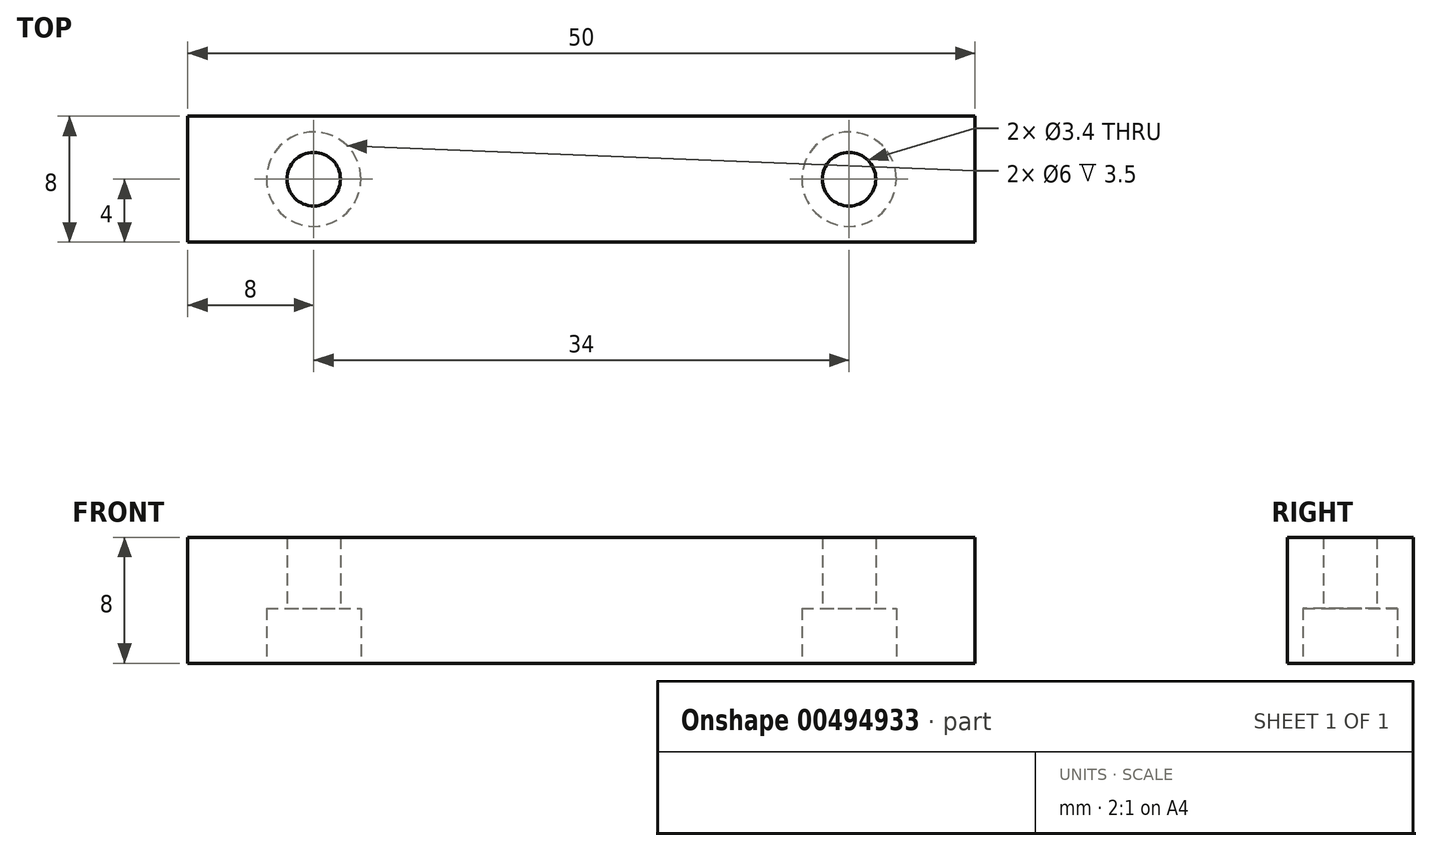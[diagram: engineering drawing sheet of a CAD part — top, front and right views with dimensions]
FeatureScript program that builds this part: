
annotation { "Feature Type Name" : "Feature", "Feature Type Description" : "" }
export const myFeature = defineFeature(function(context is Context, id is Id, definition is map)
    precondition{}
    {
        {
            var Q0;
            Q0=qCreatedBy(makeId("Top.planeOp"),FACE);
            var sketch = newSketch(context, id + "F0", { "sketchPlane" : qUnion([Q0])});
            skLineSegment(sketch, "E0.bottom", {"start": v(-8, 4) * mm, "end": v(42, 4) * mm});
            skLineSegment(sketch, "E0.top", {"start": v(-8, -4) * mm, "end": v(42, -4) * mm});
            skLineSegment(sketch, "E0.left", {"start": v(-8, 4) * mm, "end": v(-8, -4) * mm});
            skLineSegment(sketch, "E0.right", {"start": v(42, 4) * mm, "end": v(42, -4) * mm});
            skSolve(sketch);
        }
        {
            var Q0;
            Q0=qSketchRegion(id+"F0",true);
            extrude(context, id + "F1", {"entities" : qUnion([Q0]), "depth" : 8 * mm});
        }
        {
            var Q0;
            Q0=qCreatedBy(makeId("Top.planeOp"),FACE);
            var sketch = newSketch(context, id + "F2", { "sketchPlane" : qUnion([Q0])});
            skPoint(sketch, "E1", {"position": v(0, 0) * mm});
            skPoint(sketch, "E2", {"position": v(34, 0) * mm});
            skSolve(sketch);
        }
        {
            var Q0;
            Q0=sQuery(id+"F2.wireOp",VERTEX,"E1");
            var Q1;
            Q1=sQuery(id+"F2.wireOp",VERTEX,"E2");
            var Q2;
            Q2=makeQuery(id+"F1.opExtrude","SWEPT_BODY",BODY,{"disambiguationData":[OSD([sQuery(id+"F0.wireOp",EDGE,"E0.bottom"),sQuery(id+"F0.wireOp",EDGE,"E0.top"),sQuery(id+"F0.wireOp",EDGE,"E0.left"),sQuery(id+"F0.wireOp",EDGE,"E0.right")])]});
            hole(context, id + "F3", {"style" : HoleStyle.C_BORE, "endStyle" : HoleEndStyle.THROUGH, "oppositeDirection" : true, "holeDiameter" : 3.4 * mm, "cBoreDiameter" : 6 * mm, "cBoreDepth" : 3.5 * mm, "isTappedThrough" : true, "tappedDepth" : 12 * mm, "tapClearance" : 3, "locations" : qUnion([Q0, Q1]), "scope" : qUnion([Q2])});
        }
    });
